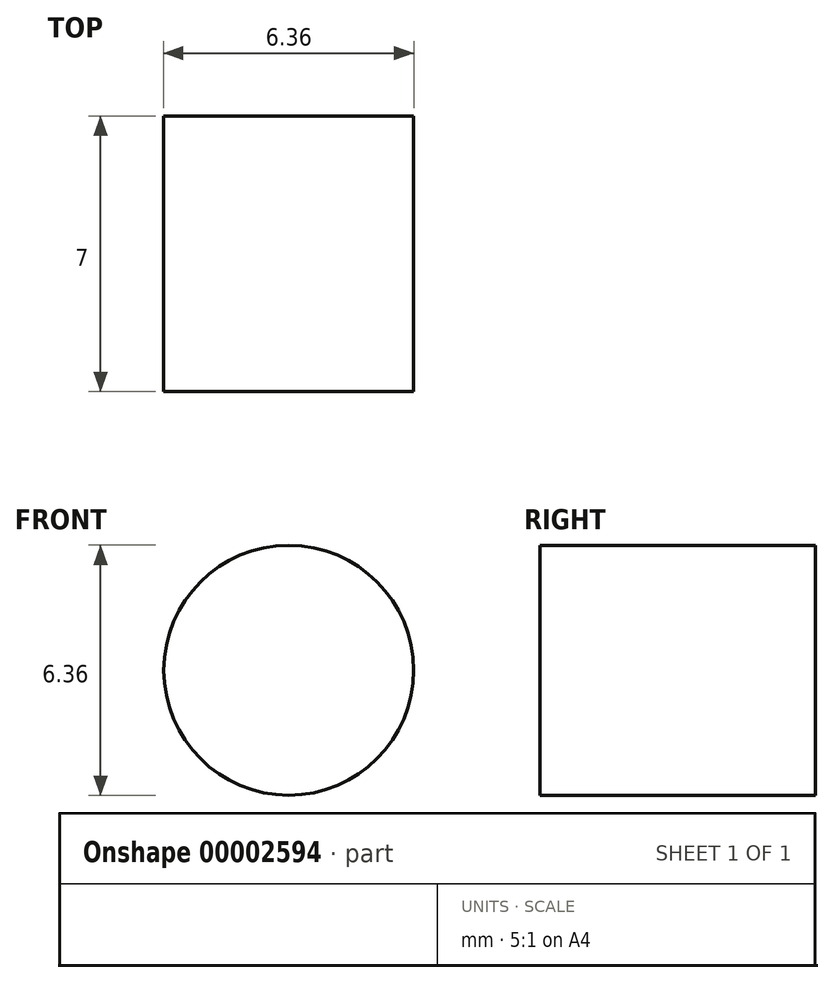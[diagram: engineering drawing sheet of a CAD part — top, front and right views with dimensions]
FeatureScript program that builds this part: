
annotation { "Feature Type Name" : "Feature", "Feature Type Description" : "" }
export const myFeature = defineFeature(function(context is Context, id is Id, definition is map)
    precondition{}
    {
        {
            var Q0;
            Q0=qCreatedBy(makeId("Front.planeOp"),FACE);
            var sketch = newSketch(context, id + "F0", { "sketchPlane" : qUnion([Q0])});
            skCircle(sketch, "E0", {"center": v(0, 0) * mm, "radius": 3.18 * mm});
            skSolve(sketch);
        }
        {
            var Q0;
            Q0 = qSketchRegion(id + "F0", true);
            extrude(context, id + "F1", {"entities" : qUnion([Q0]), "depth" : 7 * mm});
        }
    });
